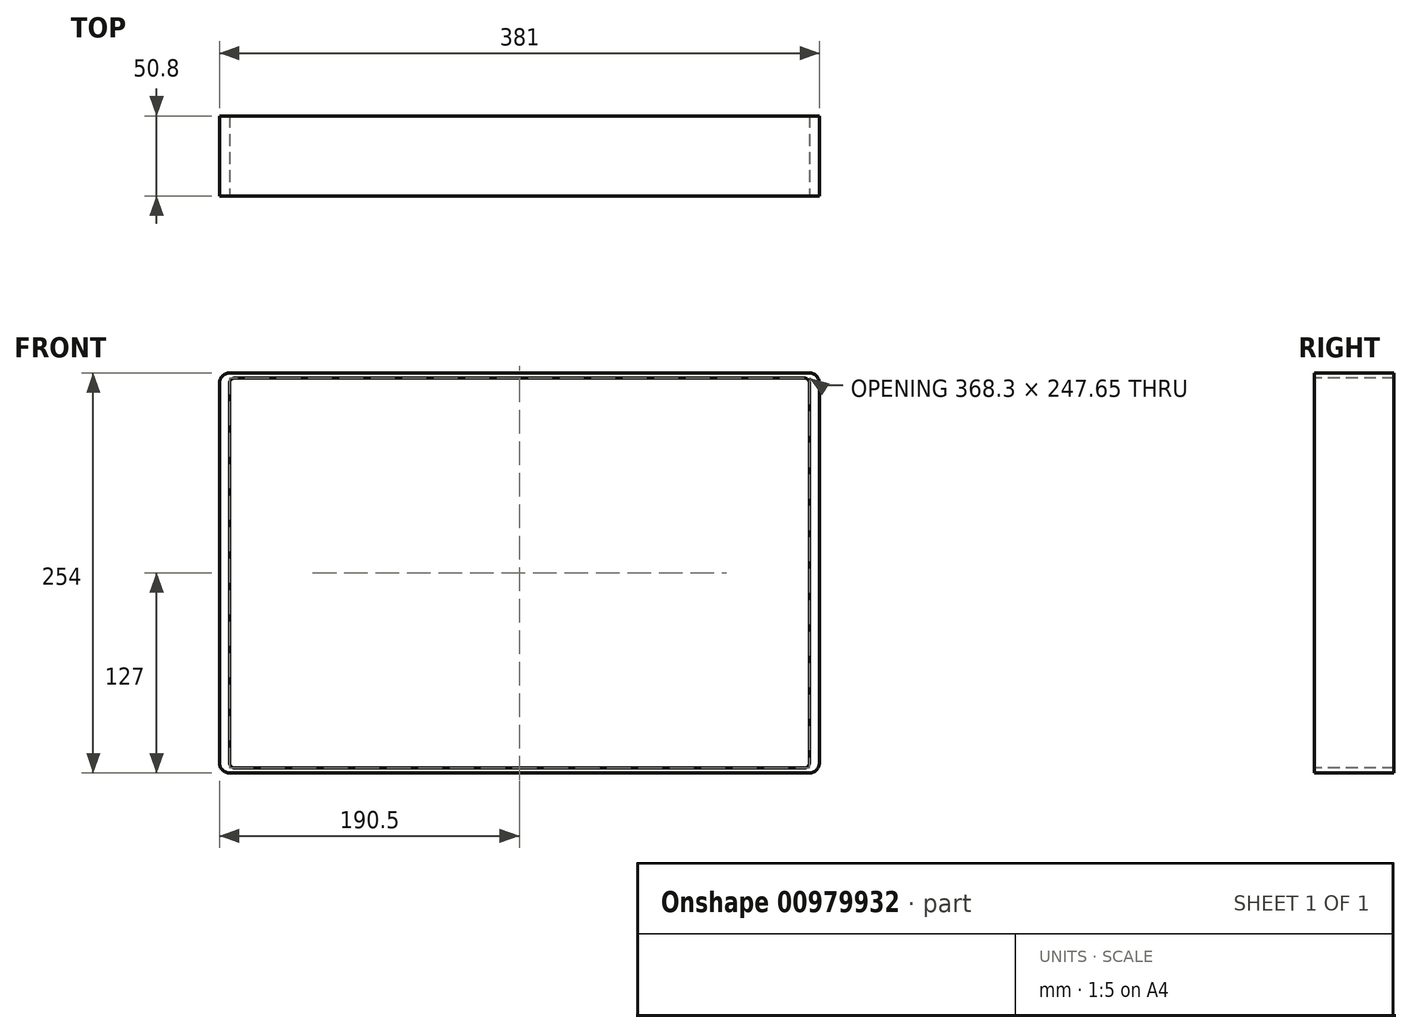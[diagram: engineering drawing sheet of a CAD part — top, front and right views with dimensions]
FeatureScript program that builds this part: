
annotation { "Feature Type Name" : "Feature", "Feature Type Description" : "" }
export const myFeature = defineFeature(function(context is Context, id is Id, definition is map)
    precondition{}
    {
        {
            var Q0;
            Q0=qCreatedBy(makeId("Front.planeOp"),FACE);
            var sketch = newSketch(context, id + "F0", { "sketchPlane" : qUnion([Q0])});
            skLineSegment(sketch, "E0.bottom", {"start": v(190.5, -127) * mm, "end": v(-190.5, -127) * mm});
            skLineSegment(sketch, "E0.top", {"start": v(190.5, 127) * mm, "end": v(-190.5, 127) * mm});
            skLineSegment(sketch, "E0.left", {"start": v(190.5, -127) * mm, "end": v(190.5, 127) * mm});
            skLineSegment(sketch, "E0.right", {"start": v(-190.5, -127) * mm, "end": v(-190.5, 127) * mm});
            skPoint(sketch, "E0.middle", {"position": v(0, 0) * mm});
            skSolve(sketch);
        }
        {
            var Q0;
            Q0=makeQuery(id+"F0.imprint","IMPRINT",FACE,{"disambiguationData":[TD([[makeQuery(id+"F0.imprint","IMPRINT",EDGE,{"derivedFrom":sQuery(id+"F0.wireOp",EDGE,"E0.bottom")}),-1.0]])]});
            extrude(context, id + "F1", {"entities" : qUnion([Q0]), "depth" : 50.8 * mm, "offsetDistance" : 25.4 * mm});
        }
        {
            var Q0;
            Q0=makeQuery(id+"F1.opExtrude","SWEPT_EDGE",EDGE,{"disambiguationData":[OSD([sQuery(id+"F0.wireOp",EDGE,"E0.top"),sQuery(id+"F0.wireOp",EDGE,"E0.left")])]});
            fillet(context, id + "F2", {"entities" : qUnion([Q0]), "radius" : 6.35 * mm, "tangentPropagation" : true, "allowEdgeOverflow" : false});
        }
        {
            var Q0;
            Q0=makeQuery(id+"F1.opExtrude","SWEPT_EDGE",EDGE,{"disambiguationData":[OSD([sQuery(id+"F0.wireOp",EDGE,"E0.bottom"),sQuery(id+"F0.wireOp",EDGE,"E0.left")])]});
            var Q1;
            Q1=makeQuery(id+"F1.opExtrude","SWEPT_EDGE",EDGE,{"disambiguationData":[OSD([sQuery(id+"F0.wireOp",EDGE,"E0.top"),sQuery(id+"F0.wireOp",EDGE,"E0.right")])]});
            var Q2;
            Q2=makeQuery(id+"F1.opExtrude","SWEPT_EDGE",EDGE,{"disambiguationData":[OSD([sQuery(id+"F0.wireOp",EDGE,"E0.bottom"),sQuery(id+"F0.wireOp",EDGE,"E0.right")])]});
            fillet(context, id + "F3", {"entities" : qUnion([Q0, Q1, Q2]), "radius" : 6.35 * mm, "tangentPropagation" : true, "allowEdgeOverflow" : false});
        }
        {
            var Q0;
            Q0=makeQuery(id+"F1.opExtrude","SWEPT_BODY",BODY,{"disambiguationData":[OSD([sQuery(id+"F0.wireOp",EDGE,"E0.bottom"),sQuery(id+"F0.wireOp",EDGE,"E0.top"),sQuery(id+"F0.wireOp",EDGE,"E0.left"),sQuery(id+"F0.wireOp",EDGE,"E0.right")])]});
            transform(context, id + "F4", {"entities" : qUnion([Q0]), "transformType" : TransformType.TRANSLATION_3D, "dx" : 0 * mm, "dy" : 50.8 * mm, "dz" : 0 * mm, "makeCopy" : false});
        }
        {
            var Q0;
            Q0=qCreatedBy(makeId("Front.planeOp"),FACE);
            var sketch = newSketch(context, id + "F5", { "sketchPlane" : qUnion([Q0])});
            skLineSegment(sketch, "E1.bottom", {"start": v(184.15, -123.83) * mm, "end": v(-184.15, -123.83) * mm});
            skLineSegment(sketch, "E1.top", {"start": v(184.15, 123.83) * mm, "end": v(-184.15, 123.82) * mm});
            skLineSegment(sketch, "E1.left", {"start": v(184.15, -123.83) * mm, "end": v(184.15, 123.83) * mm});
            skLineSegment(sketch, "E1.right", {"start": v(-184.15, -123.83) * mm, "end": v(-184.15, 123.82) * mm});
            skPoint(sketch, "E1.middle", {"position": v(0, 0) * mm});
            skSolve(sketch);
        }
        {
            var Q0;
            Q0=makeQuery(id+"F5.imprint","IMPRINT",FACE,{"disambiguationData":[TD([[makeQuery(id+"F5.imprint","IMPRINT",EDGE,{"derivedFrom":sQuery(id+"F5.wireOp",EDGE,"E1.bottom")}),-1.0]])]});
            extrude(context, id + "F6", {"entities" : qUnion([Q0]), "operationType" : NewBodyOperationType.REMOVE, "oppositeDirection" : true, "depth" : 50.8 * mm, "offsetDistance" : 25.4 * mm});
        }
        {
            var Q0;
            Q0=makeQuery(id+"F6.boolean.opBoolean","COPY",EDGE,{"derivedFrom":makeQuery(id+"F6.opExtrude","SWEPT_EDGE",EDGE,{"disambiguationData":[OSD([sQuery(id+"F5.wireOp",EDGE,"E1.bottom"),sQuery(id+"F5.wireOp",EDGE,"E1.left")])]})});
            var Q1;
            Q1=makeQuery(id+"F6.boolean.opBoolean","COPY",EDGE,{"derivedFrom":makeQuery(id+"F6.opExtrude","SWEPT_EDGE",EDGE,{"disambiguationData":[OSD([sQuery(id+"F5.wireOp",EDGE,"E1.top"),sQuery(id+"F5.wireOp",EDGE,"E1.left")])]})});
            var Q2;
            Q2=makeQuery(id+"F6.boolean.opBoolean","COPY",EDGE,{"derivedFrom":makeQuery(id+"F6.opExtrude","SWEPT_EDGE",EDGE,{"disambiguationData":[OSD([sQuery(id+"F5.wireOp",EDGE,"E1.top"),sQuery(id+"F5.wireOp",EDGE,"E1.right")])]})});
            var Q3;
            Q3=makeQuery(id+"F6.boolean.opBoolean","COPY",EDGE,{"derivedFrom":makeQuery(id+"F6.opExtrude","SWEPT_EDGE",EDGE,{"disambiguationData":[OSD([sQuery(id+"F5.wireOp",EDGE,"E1.bottom"),sQuery(id+"F5.wireOp",EDGE,"E1.right")])]})});
            fillet(context, id + "F7", {"entities" : qUnion([Q0, Q1, Q2, Q3]), "radius" : 3.17 * mm, "tangentPropagation" : true, "allowEdgeOverflow" : false});
        }
        {
            var Q0;
            Q0=makeQuery(id+"F1.opExtrude","SWEPT_BODY",BODY,{"disambiguationData":[OSD([sQuery(id+"F0.wireOp",EDGE,"E0.bottom"),sQuery(id+"F0.wireOp",EDGE,"E0.top"),sQuery(id+"F0.wireOp",EDGE,"E0.left"),sQuery(id+"F0.wireOp",EDGE,"E0.right")])]});
            transform(context, id + "F8", {"entities" : qUnion([Q0]), "transformType" : TransformType.TRANSLATION_3D, "dx" : 0 * mm, "dy" : 50.8 * mm, "dz" : 0 * mm, "makeCopy" : false});
        }
        {
            var Q0;
            Q0=makeQuery(id+"F1.opExtrude","SWEPT_BODY",BODY,{"disambiguationData":[OSD([sQuery(id+"F0.wireOp",EDGE,"E0.bottom"),sQuery(id+"F0.wireOp",EDGE,"E0.top"),sQuery(id+"F0.wireOp",EDGE,"E0.left"),sQuery(id+"F0.wireOp",EDGE,"E0.right")])]});
            transform(context, id + "F9", {"entities" : qUnion([Q0]), "transformType" : TransformType.TRANSLATION_3D, "dx" : 0 * mm, "dy" : 0 * mm, "dz" : -101.6 * mm, "makeCopy" : false});
        }
        {
            var Q0;
            Q0=makeQuery(id+"F1.opExtrude","SWEPT_BODY",BODY,{"disambiguationData":[OSD([sQuery(id+"F0.wireOp",EDGE,"E0.bottom"),sQuery(id+"F0.wireOp",EDGE,"E0.top"),sQuery(id+"F0.wireOp",EDGE,"E0.left"),sQuery(id+"F0.wireOp",EDGE,"E0.right")])]});
            transform(context, id + "F10", {"entities" : qUnion([Q0]), "transformType" : TransformType.TRANSLATION_3D, "dx" : 0 * mm, "dy" : 203.2 * mm, "dz" : 0 * mm, "makeCopy" : false});
        }
        {
            var Q0;
            Q0=makeQuery(id+"F1.opExtrude","SWEPT_BODY",BODY,{"disambiguationData":[OSD([sQuery(id+"F0.wireOp",EDGE,"E0.bottom"),sQuery(id+"F0.wireOp",EDGE,"E0.top"),sQuery(id+"F0.wireOp",EDGE,"E0.left"),sQuery(id+"F0.wireOp",EDGE,"E0.right")])]});
            transform(context, id + "F11", {"entities" : qUnion([Q0]), "transformType" : TransformType.TRANSLATION_3D, "dx" : 0 * mm, "dy" : 0 * mm, "dz" : 203.2 * mm, "makeCopy" : false});
        }
    });
